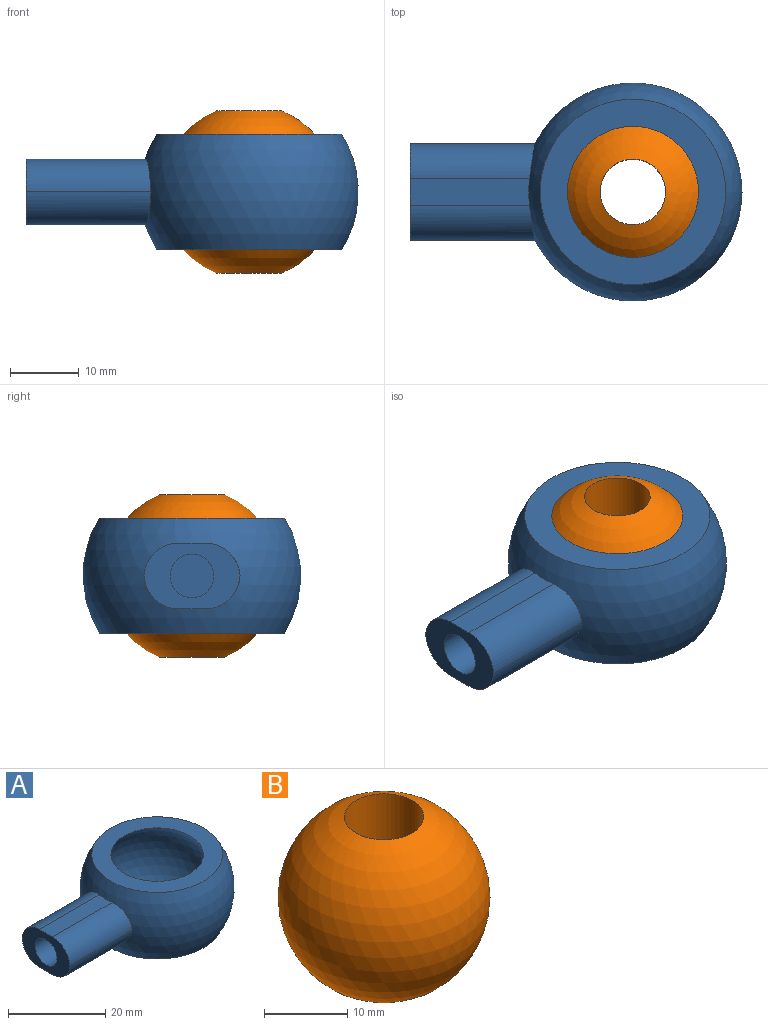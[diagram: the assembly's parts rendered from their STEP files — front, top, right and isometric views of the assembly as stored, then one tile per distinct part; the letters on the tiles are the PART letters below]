
ASSEMBLY  parts=2 mates=1
PART A: 13 faces, bbox 48.3x31.8x16.8 mm
  f0: plane 26.94x26.94mm, normal (0,0,1), area 285mm2, adj f1,f3
  f1: sphere r=15.88mm, area 1560.4mm2, adj f0,f2,f4,f6,f7,f8,f9,f10
  f2: plane 26.94x26.94mm, normal (0,0,-1), area 285mm2, adj f1,f3
  f3: sphere r=12.7mm, area 1340.6mm2, adj f0,f2
  f4: plane 17.36x3.81mm, normal (0,0,1), area 65.8mm2, adj f1,f5,f8,f10
  f5: plane 13.95x9.53mm, normal (-1,0,0), area 79.2mm2, adj f4,f6,f7,f8,f9,f10,f11
  f6: plane 17.35x3.81mm, normal (0,0,-1), area 65.8mm2, adj f1,f5,f7,f9
  f7: cylinder r=5.08mm len=18.12mm, axis (1,0,0), area 136.4mm2, adj f1,f5,f6,f8
  f8: cylinder r=5.08mm len=18.12mm, axis (-1,0,0), area 136.4mm2, adj f1,f4,f5,f7
  f9: cylinder r=5.08mm len=18.12mm, axis (-1,0,0), area 136.4mm2, adj f1,f5,f6,f10
  f10: cylinder r=5.08mm len=18.12mm, axis (1,0,0), area 136.4mm2, adj f1,f4,f5,f9
  f11: cylinder r=3.17mm len=6.35mm, axis (-1,0,0), area 126.7mm2, adj f5,f12
  f12: plane 6.35x6.35mm, normal (-1,0,0), area 31.7mm2, adj f11
PART B: 2 faces, bbox 25.4x25.4x23.5 mm
  f0: cylinder r=4.76mm len=23.55mm, axis (0,0,1), area 704.6mm2, adj f1
  f1: sphere r=12.7mm, area 1878.9mm2, adj f0
PLACE A t=(175.56,-63.86,4.63)mm
PLACE B t=(96.56,-63.86,13.18)mm
MATE ball B.f0 <-> A.f1  axis (0,0,1) through (-70.18,-63.86,-27.86)mm
